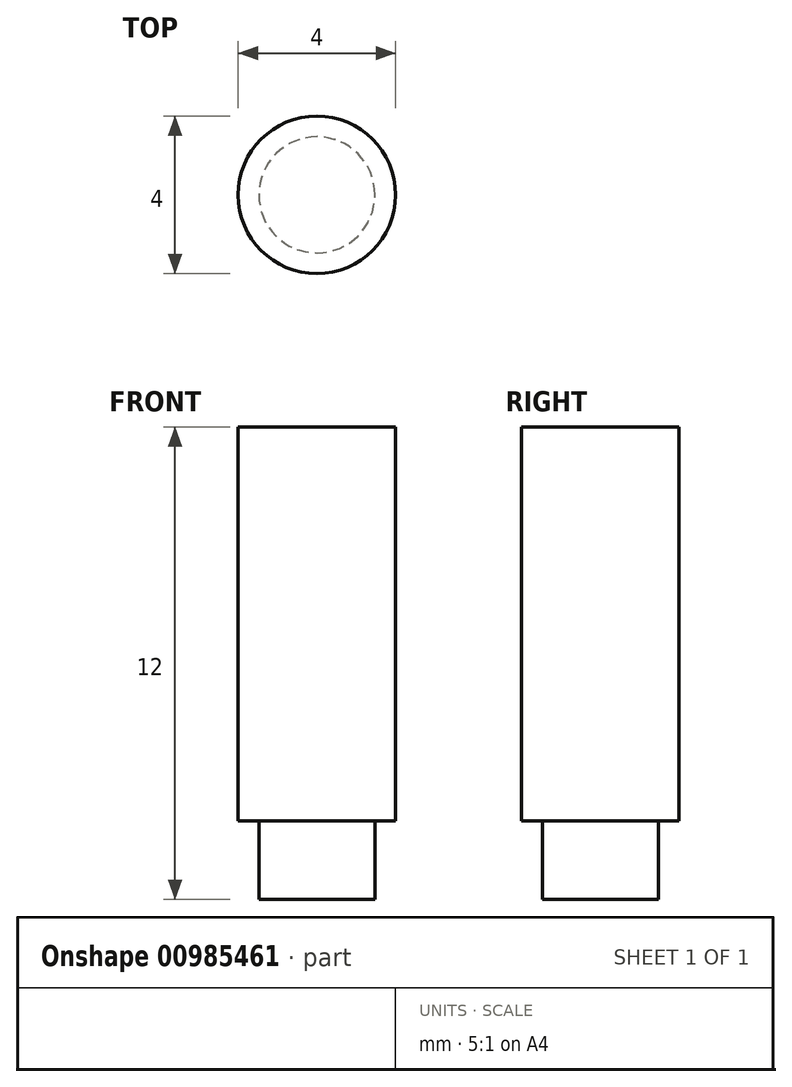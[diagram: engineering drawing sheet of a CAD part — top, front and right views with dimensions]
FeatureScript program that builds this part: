
annotation { "Feature Type Name" : "Feature", "Feature Type Description" : "" }
export const myFeature = defineFeature(function(context is Context, id is Id, definition is map)
    precondition{}
    {
        {
            var Q0;
            Q0=qCreatedBy(makeId("Top.planeOp"),FACE);
            var sketch = newSketch(context, id + "F0", { "sketchPlane" : qUnion([Q0])});
            skLineSegment(sketch, "E0", {"start": v(0, 0) * mm, "end": v(0, -10) * mm, "construction": true});
            skCircle(sketch, "E1", {"center": v(0, -10) * mm, "radius": 1.48 * mm});
            skSolve(sketch);
        }
        {
            var Q0;
            Q0 = qSketchRegion(id + "F0", true);
            extrude(context, id + "F1", {"entities" : qUnion([Q0]), "depth" : 2 * mm, "offsetDistance" : 25 * mm});
        }
        {
            var Q0;
            Q0=makeQuery(id+"F1.opExtrude","CAP_FACE",FACE,{"disambiguationData":[OSD([sQuery(id+"F0.wireOp",EDGE,"E1")])],"isStart":false});
            var sketch = newSketch(context, id + "F2", { "sketchPlane" : qUnion([Q0])});
            skCircle(sketch, "E2", {"center": v(0, -10) * mm, "radius": 2 * mm});
            skSolve(sketch);
        }
        {
            var Q0;
            Q0 = qSketchRegion(id + "F2", true);
            extrude(context, id + "F3", {"entities" : qUnion([Q0]), "operationType" : NewBodyOperationType.ADD, "depth" : 10 * mm, "offsetDistance" : 25 * mm});
        }
    });
